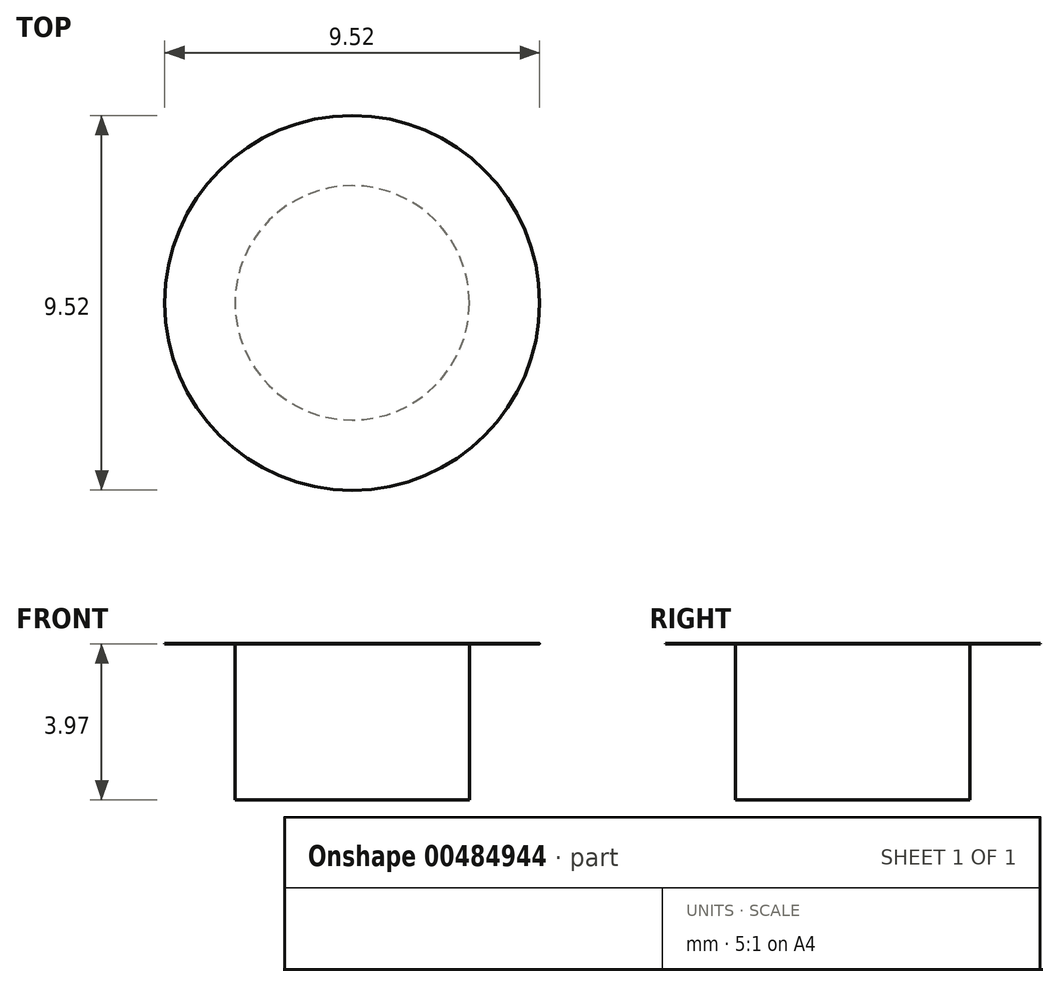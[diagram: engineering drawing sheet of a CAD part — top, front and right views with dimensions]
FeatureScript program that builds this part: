
annotation { "Feature Type Name" : "Feature", "Feature Type Description" : "" }
export const myFeature = defineFeature(function(context is Context, id is Id, definition is map)
    precondition{}
    {
        {
            var Q0;
            Q0=qCreatedBy(makeId("Top.planeOp"),FACE);
            var sketch = newSketch(context, id + "F0", { "sketchPlane" : qUnion([Q0])});
            skCircle(sketch, "E0", {"center": v(0, 0) * mm, "radius": 2.98 * mm});
            skSolve(sketch);
        }
        {
            var Q0;
            Q0 = qSketchRegion(id + "F0", true);
            extrude(context, id + "F1", {"entities" : qUnion([Q0]), "depth" : 3.97 * mm});
        }
        {
            var Q0;
            Q0=makeQuery(id+"F1.opExtrude","CAP_FACE",FACE,{"disambiguationData":[OSD([sQuery(id+"F0.wireOp",EDGE,"E0")])],"isStart":false});
            var sketch = newSketch(context, id + "F2", { "sketchPlane" : qUnion([Q0])});
            skCircle(sketch, "E1", {"center": v(0, 0) * mm, "radius": 4.76 * mm});
            skSolve(sketch);
        }
        {
            var Q0;
            Q0 = qSketchRegion(id + "F2", true);
            extrude(context, id + "F3", {"entities" : qUnion([Q0]), "operationType" : NewBodyOperationType.ADD, "depth" : 1 / 406.4 * mm});
        }
    });
